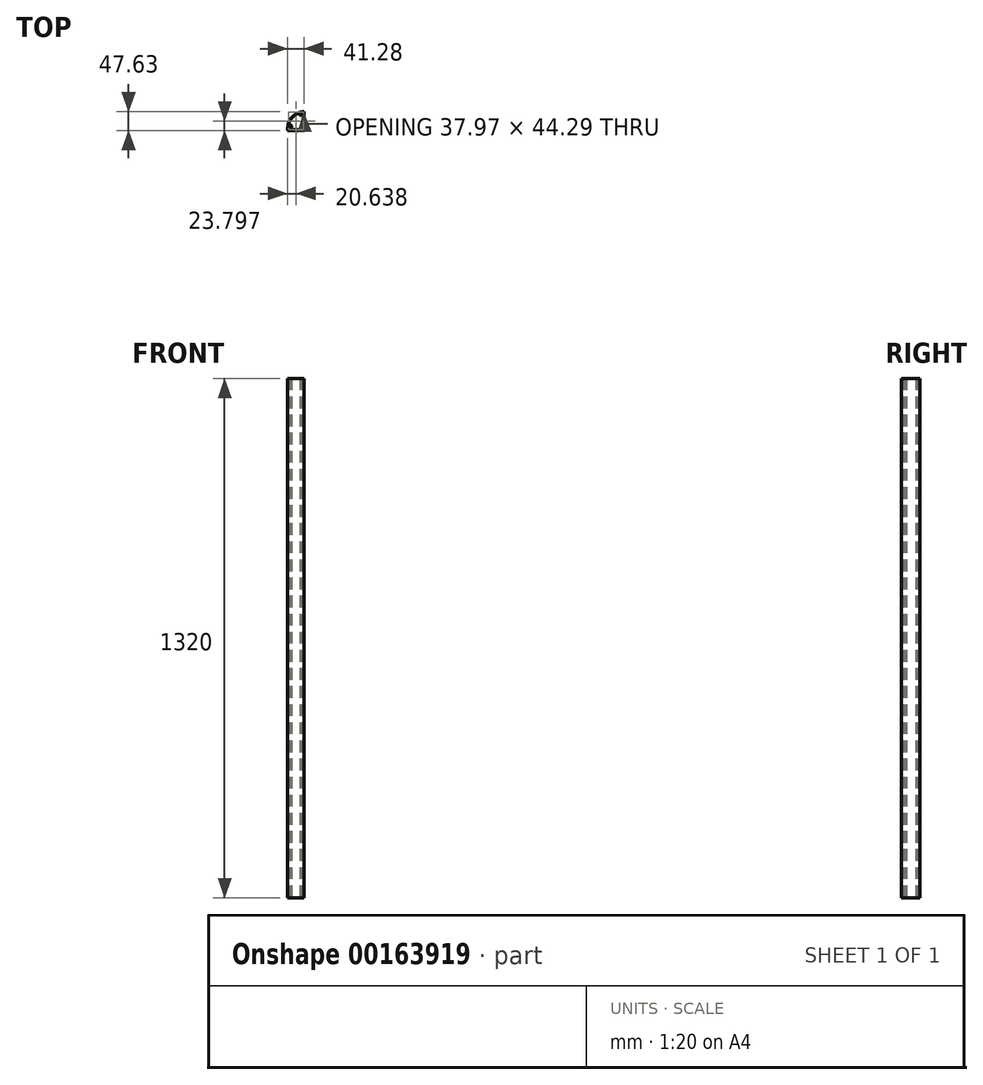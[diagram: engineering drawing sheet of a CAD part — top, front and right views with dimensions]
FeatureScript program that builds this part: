
annotation { "Feature Type Name" : "Feature", "Feature Type Description" : "" }
export const myFeature = defineFeature(function(context is Context, id is Id, definition is map)
    precondition{}
    {
        {
            var Q0;
            Q0=qCreatedBy(makeId("Top.planeOp"),FACE);
            var sketch = newSketch(context, id + "F0", { "sketchPlane" : qUnion([Q0])});
            skArc(sketch, "E0", {"start": v(30.01, 44.37) * mm, "mid": v(31.6, 43.8) * mm, "end": v(31.48, 42.11) * mm});
            skArc(sketch, "E1", {"start": v(31.48, 42.11) * mm, "mid": v(30.76, 40.02) * mm, "end": v(31.64, 37.99) * mm});
            skArc(sketch, "E2", {"start": v(31.64, 37.99) * mm, "mid": v(32.53, 37.98) * mm, "end": v(32.54, 38.88) * mm});
            skArc(sketch, "E3", {"start": v(32.54, 38.88) * mm, "mid": v(33.8, 41.91) * mm, "end": v(35.06, 38.88) * mm});
            skArc(sketch, "E4", {"start": v(35.06, 38.88) * mm, "mid": v(35.07, 37.98) * mm, "end": v(35.97, 37.99) * mm});
            skArc(sketch, "E5", {"start": v(35.97, 37.99) * mm, "mid": v(36.8, 40.69) * mm, "end": v(35.06, 42.91) * mm});
            skArc(sketch, "E6", {"start": v(35.06, 42.91) * mm, "mid": v(34.24, 44.38) * mm, "end": v(35.43, 45.58) * mm});
            skArc(sketch, "E7", {"start": v(35.43, 45.58) * mm, "mid": v(37.55, 45.84) * mm, "end": v(39.7, 46) * mm});
            skLineSegment(sketch, "E8", {"start": v(39.7, 46) * mm, "end": v(39.7, 1.7) * mm});
            skLineSegment(sketch, "E9", {"start": v(39.7, 1.7) * mm, "end": v(1.72, 1.7) * mm});
            skLineSegment(sketch, "E10", {"start": v(1.72, 1.7) * mm, "end": v(1.72, 6.4) * mm});
            skArc(sketch, "E11", {"start": v(1.72, 6.4) * mm, "mid": v(1.73, 7.02) * mm, "end": v(1.74, 7.64) * mm});
            skArc(sketch, "E12", {"start": v(1.74, 7.64) * mm, "mid": v(3.06, 9.32) * mm, "end": v(5.05, 8.56) * mm});
            skArc(sketch, "E13", {"start": v(5.05, 8.56) * mm, "mid": v(7.28, 7.18) * mm, "end": v(9.76, 8.05) * mm});
            skArc(sketch, "E14", {"start": v(9.76, 8.05) * mm, "mid": v(9.76, 8.95) * mm, "end": v(8.87, 8.95) * mm});
            skArc(sketch, "E15", {"start": v(8.87, 8.95) * mm, "mid": v(5.84, 10.21) * mm, "end": v(8.87, 11.48) * mm});
            skArc(sketch, "E16", {"start": v(8.87, 11.48) * mm, "mid": v(9.76, 11.48) * mm, "end": v(9.76, 12.38) * mm});
            skArc(sketch, "E17", {"start": v(9.76, 12.38) * mm, "mid": v(7.63, 13.26) * mm, "end": v(5.49, 12.4) * mm});
            skArc(sketch, "E18", {"start": v(5.49, 12.4) * mm, "mid": v(3.37, 12.1) * mm, "end": v(2.46, 14.03) * mm});
            skArc(sketch, "E19", {"start": v(2.46, 14.03) * mm, "mid": v(12.01, 33.04) * mm, "end": v(30.01, 44.37) * mm});
            skLineSegment(sketch, "E20", {"start": v(0.07, 0.05) * mm, "end": v(41.35, 0.05) * mm});
            skArc(sketch, "E21", {"start": v(41.35, 47.68) * mm, "mid": v(12.16, 35.59) * mm, "end": v(0.07, 6.4) * mm});
            skLineSegment(sketch, "E22", {"start": v(0.07, 6.4) * mm, "end": v(0.07, 0.05) * mm});
            skLineSegment(sketch, "E23", {"start": v(41.35, 0.05) * mm, "end": v(41.35, 47.68) * mm});
            skSolve(sketch);
        }
        {
            var Q0;
            Q0=makeQuery(id+"F0.imprint","IMPRINT",FACE,{"disambiguationData":[TD([[makeQuery(id+"F0.imprint","IMPRINT",EDGE,{"derivedFrom":sQuery(id+"F0.wireOp",EDGE,"E13")}),1.0]])]});
            extrude(context, id + "F1", {"entities" : qUnion([Q0]), "depth" : 1320 * mm});
        }
    });
